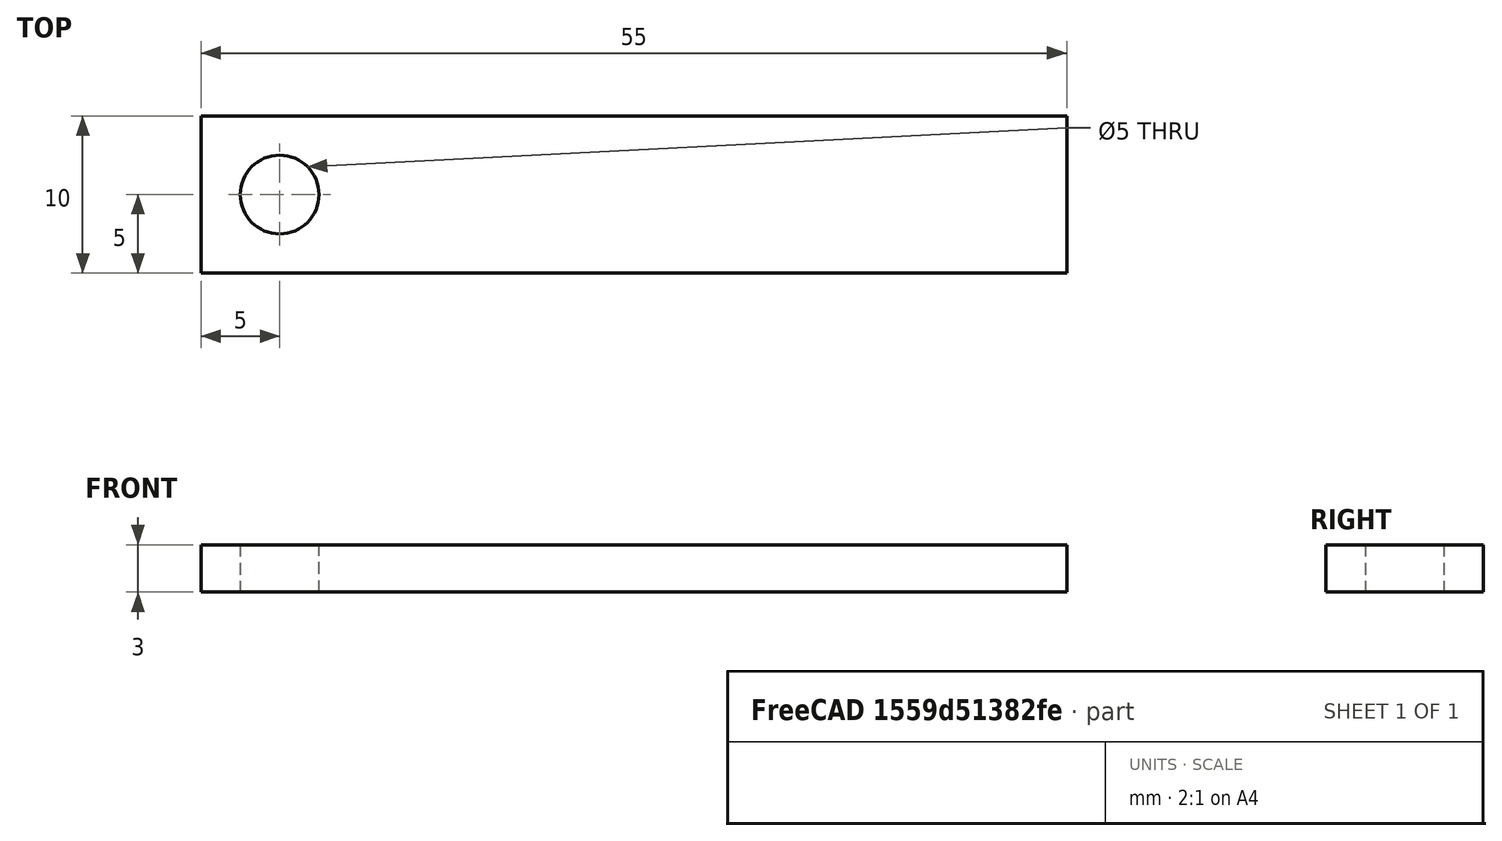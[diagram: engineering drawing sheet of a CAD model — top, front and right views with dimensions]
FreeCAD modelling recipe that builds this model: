
FCSTD DOCUMENT  (FreeCAD 0.20R29410 (Git))
Label: Rectangle
License: All rights reserved
LicenseURL: http://en.wikipedia.org/wiki/All_rights_reserved
objects: Sketcher::SketchObject×1, Part::Extrusion×1, PartDesign::Line×1, App::Part×1
note: 3 computed .brp shape members not serialized (recipe doc carries the construction recipe); baked Part::Feature solids carry a one-line shape summary decoded from their .brp

FEATURE [Sketcher::SketchObject] Sketch
  FullyConstrained = true
  sketch-geometry (5):
    g0: LineSegment StartX=-27.5 StartY=5 StartZ=0 EndX=27.5 EndY=5 EndZ=0
    g1: LineSegment StartX=27.5 StartY=5 StartZ=0 EndX=27.5 EndY=-5 EndZ=0
    g2: LineSegment StartX=27.5 StartY=-5 StartZ=0 EndX=-27.5 EndY=-5 EndZ=0
    g3: LineSegment StartX=-27.5 StartY=-5 StartZ=0 EndX=-27.5 EndY=5 EndZ=0
    g4: Circle CenterX=-22.5 CenterY=0 CenterZ=0 NormalX=0 NormalY=0 NormalZ=1 AngleXU=0 Radius=2.5
  constraints (14):
    c: Coincident(g0,g1)
    c: Coincident(g1,g2)
    c: Coincident(g2,g3)
    c: Coincident(g3,g0)
    c: Horizontal(g0)
    c: Horizontal(g2)
    c: Vertical(g1)
    c: Vertical(g3)
    c: Symmetric(g0,g2,g-1)
    c: DistanceX(g0,g0) = 55
    c: DistanceY(g1,g1) = 10
    c: Diameter(g4) = 5
    c: DistanceX(g0,g4) = 5
    c: PointOnObject(g4,g-1)
FEATURE [Part::Extrusion] Extrude
  Base = -> Sketch
  Dir = (0,0,1)
  DirMode = 2
  FaceMakerClass = Part::FaceMakerBullseye
  LengthFwd = 3
  LengthRev = 0
  Solid = true
  Symmetric = false
FEATURE [PartDesign::Line] HoleAxis_1
  AttacherType = Attacher::AttachEngineLine
  Length = 7.04534
  MapMode = 19
  Placement = pos=(-22.5,0,3) rot=(0,0,1;0rad)
  ResizeMode = 1
  Support = -> [Extrude]
FEATURE [App::Part] Part  label="RectanglePart"
  Group = -> [Sketch,Extrude,HoleAxis_1]
  Origin = -> Origin
